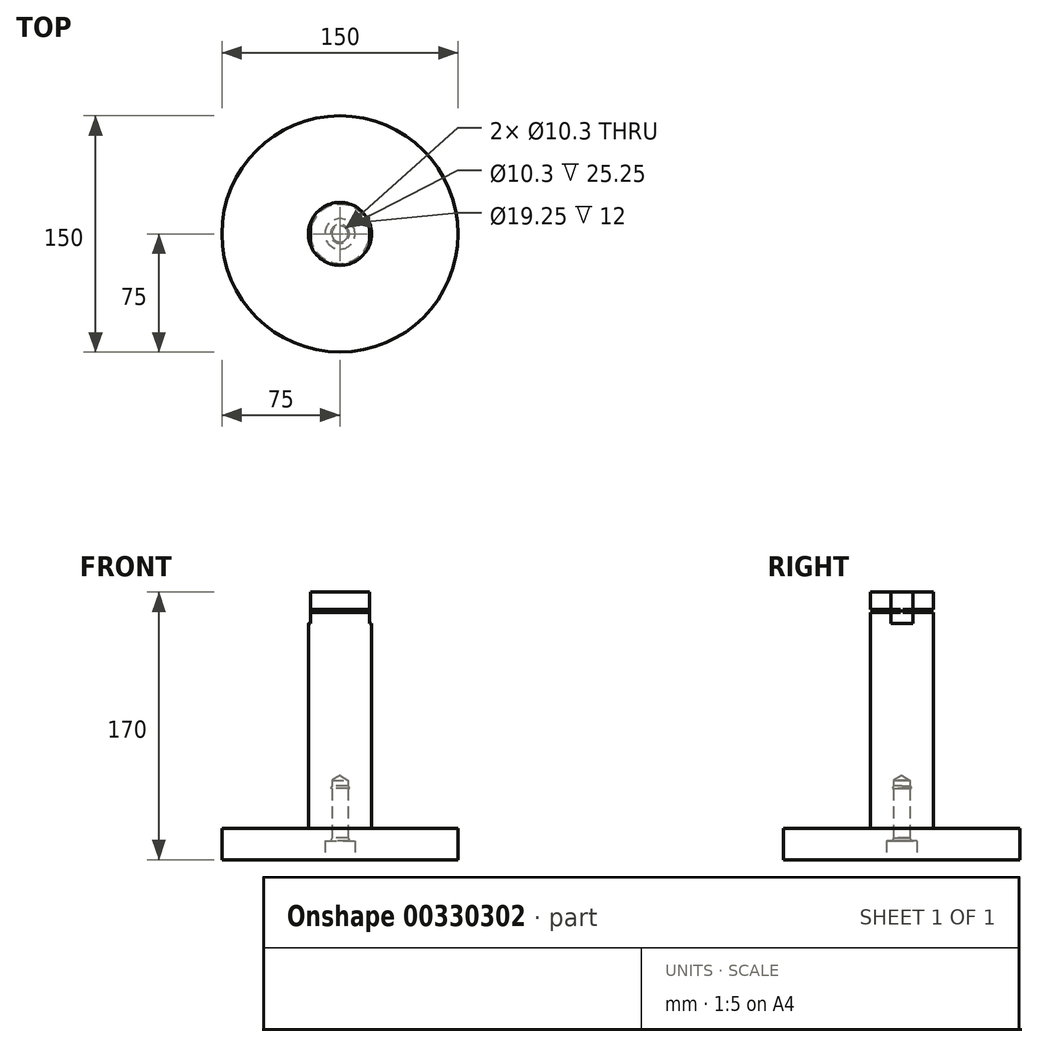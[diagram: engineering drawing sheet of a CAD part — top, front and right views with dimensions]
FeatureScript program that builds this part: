
annotation { "Feature Type Name" : "Feature", "Feature Type Description" : "" }
export const myFeature = defineFeature(function(context is Context, id is Id, definition is map)
    precondition{}
    {
        {
            var Q0;
            Q0=qCreatedBy(makeId("Top.planeOp"),FACE);
            var sketch = newSketch(context, id + "F0", { "sketchPlane" : qUnion([Q0])});
            skCircle(sketch, "E0", {"center": v(0, 0) * mm, "radius": 20 * mm});
            skCircle(sketch, "E1", {"center": v(0, 0) * mm, "radius": 75 * mm});
            skSolve(sketch);
        }
        {
            var Q0;
            Q0=makeQuery(id+"F0.imprint","IMPRINT",FACE,{"disambiguationData":[TD([[makeQuery(id+"F0.imprint","IMPRINT",EDGE,{"derivedFrom":sQuery(id+"F0.wireOp",EDGE,"E0")}),-1.0]])]});
            var Q1;
            Q1=makeQuery(id+"F0.imprint","IMPRINT",FACE,{"disambiguationData":[TD([[makeQuery(id+"F0.imprint","IMPRINT",EDGE,{"derivedFrom":sQuery(id+"F0.wireOp",EDGE,"E0")}),1.0]])]});
            extrude(context, id + "F1", {"entities" : qUnion([Q0, Q1]), "oppositeDirection" : true, "depth" : 20 * mm});
        }
        {
            var Q0;
            Q0=makeQuery(id+"F0.imprint","IMPRINT",FACE,{"disambiguationData":[TD([[makeQuery(id+"F0.imprint","IMPRINT",EDGE,{"derivedFrom":sQuery(id+"F0.wireOp",EDGE,"E0")}),1.0]])]});
            extrude(context, id + "F2", {"entities" : qUnion([Q0]), "depth" : 150 * mm});
        }
        {
            var Q0;
            Q0=makeQuery(id+"F1.opExtrude","CAP_FACE",FACE,{"disambiguationData":[OSD([sQuery(id+"F0.wireOp",EDGE,"E1")])],"isStart":false});
            var sketch = newSketch(context, id + "F3", { "sketchPlane" : qUnion([Q0])});
            skPoint(sketch, "E2", {"position": v(0, 0) * mm});
            skSolve(sketch);
        }
        {
            var Q0;
            Q0=sQuery(id+"F3.wireOp",VERTEX,"E2");
            var Q1;
            Q1=makeQuery(id+"F1.opExtrude","SWEPT_BODY",BODY,{"disambiguationData":[OSD([sQuery(id+"F0.wireOp",EDGE,"E1")])]});
            var Q2;
            Q2=makeQuery(id+"F2.opExtrude","SWEPT_BODY",BODY,{"disambiguationData":[OSD([sQuery(id+"F0.wireOp",EDGE,"E0")])]});
            hole(context, id + "F4", {"style" : HoleStyle.C_BORE, "endStyle" : HoleEndStyle.BLIND, "standardTappedOrClearance" : lookupTablePath({ "standard" : "ISO", "engagement" : "75%", "pitch" : "1.75 mm", "size" : "M12", "type" : "Tapped" }), "standardBlindInLast" : lookupTablePath({ "standard" : "ISO", "engagement" : "75%", "pitch" : "1.75 mm", "size" : "M12", "type" : "Tapped" }), "holeDiameter" : 10.3 * mm, "cBoreDiameter" : 19.25 * mm, "cBoreDepth" : 12 * mm, "showTappedDepth" : true, "holeDepth" : 50.5 * mm, "tappedDepth" : 47 * mm, "tapClearance" : 2, "locations" : qUnion([Q0]), "scope" : qUnion([Q1, Q2]), "majorDiameter" : 12 * mm});
        }
        {
            var Q0;
            Q0=qCreatedBy(makeId("Right.planeOp"),FACE);
            var sketch = newSketch(context, id + "F5", { "sketchPlane" : qUnion([Q0])});
            skLineSegment(sketch, "E3.0", {"start": v(9.62, -8) * mm, "end": v(-9.62, -8) * mm});
            skLineSegment(sketch, "E4", {"start": v(0, 0) * mm, "end": v(0, -13.23) * mm});
            skLineSegment(sketch, "E5", {"start": v(0, -8) * mm, "end": v(6, -8) * mm});
            skLineSegment(sketch, "E6.MirrorCS", {"start": v(0, -16) * mm, "end": v(0, -2.77) * mm});
            skLineSegment(sketch, "E7.MirrorCS", {"start": v(0, -8) * mm, "end": v(-6, -8) * mm});
            skLineSegment(sketch, "E8", {"start": v(5.15, -8) * mm, "end": v(5.15, -6.25) * mm});
            skLineSegment(sketch, "E9", {"start": v(5.15, -6.25) * mm, "end": v(6, -8) * mm});
            skLineSegment(sketch, "E10", {"start": v(6, -8) * mm, "end": v(5.15, -8) * mm});
            skLineSegment(sketch, "E11", {"start": v(0, -8) * mm, "end": v(0, 1.54) * mm});
            skLineSegment(sketch, "E12.0", {"start": v(-75, -20) * mm, "end": v(75, -20) * mm});
            skLineSegment(sketch, "E13", {"start": v(0, -20) * mm, "end": v(0, 27) * mm});
            skLineSegment(sketch, "E14", {"start": v(0, 27) * mm, "end": v(6, 27) * mm});
            skLineSegment(sketch, "E15", {"start": v(5.15, 25.25) * mm, "end": v(5.15, 27) * mm});
            skLineSegment(sketch, "E16", {"start": v(5.15, 27) * mm, "end": v(6, 25.25) * mm});
            skLineSegment(sketch, "E17", {"start": v(6, 25.25) * mm, "end": v(5.15, 25.25) * mm});
            skSolve(sketch);
        }
        {
            var Q0;
            Q0 = qSketchRegion(id + "F5", true);
            var Q1;
            Q1=sQuery(id+"F5.wireOp",EDGE,"E13");
            revolve(context, id + "F6", {"operationType" : NewBodyOperationType.REMOVE, "entities" : qUnion([Q0]), "axis" : qUnion([Q1]), "revolveType" : RevolveType.FULL, "oppositeDirection" : true});
        }
        {
            var Q0;
            Q0=makeQuery(id+"F2.opExtrude","CAP_FACE",FACE,{"disambiguationData":[OSD([sQuery(id+"F0.wireOp",EDGE,"E0")])],"isStart":false});
            var sketch = newSketch(context, id + "F7", { "sketchPlane" : qUnion([Q0])});
            skLineSegment(sketch, "E18", {"start": v(0, 0) * mm, "end": v(-20, 0) * mm});
            skLineSegment(sketch, "E19", {"start": v(-18.73, 7) * mm, "end": v(-18.73, 0) * mm});
            skLineSegment(sketch, "E20.MirrorCS", {"start": v(-18.73, -7) * mm, "end": v(-18.73, 0) * mm});
            skLineSegment(sketch, "E21.MirrorCS", {"start": v(18.73, 7) * mm, "end": v(18.73, 0) * mm});
            skLineSegment(sketch, "E22.MirrorCS", {"start": v(18.73, -7) * mm, "end": v(18.73, 0) * mm});
            skSolve(sketch);
        }
        {
            var Q0;
            {var subQ3=sQuery(id+"F7.wireOp",EDGE,"E19");Q0=makeQuery(id+"F7.imprint","IMPRINT",FACE,{"disambiguationData":[TD([[makeQuery(id+"F7.imprint","IMPRINT",EDGE,{"derivedFrom":subQ3}),-1.0]])]});}
            var Q1;
            {var subQ3=sQuery(id+"F7.wireOp",EDGE,"E20.MirrorCS");Q1=makeQuery(id+"F7.imprint","IMPRINT",FACE,{"disambiguationData":[TD([[makeQuery(id+"F7.imprint","IMPRINT",EDGE,{"derivedFrom":subQ3}),1.0]])]});}
            var Q2;
            {var subQ0=sQuery(id+"F7.wireOp",EDGE,"E21.MirrorCS");Q2=makeQuery(id+"F7.imprint","IMPRINT",FACE,{"disambiguationData":[TD([[makeQuery(id+"F7.imprint","IMPRINT",EDGE,{"derivedFrom":subQ0}),1.0]])]});}
            extrude(context, id + "F8", {"entities" : qUnion([Q0, Q1, Q2]), "operationType" : NewBodyOperationType.REMOVE, "oppositeDirection" : true, "depth" : 20 * mm});
        }
        {
            var Q0;
            Q0=makeQuery(id+"F0.imprint","IMPRINT",FACE,{"disambiguationData":[TD([[makeQuery(id+"F0.imprint","IMPRINT",EDGE,{"derivedFrom":sQuery(id+"F0.wireOp",EDGE,"E0")}),-1.0]])]});
            cPlane(context, id + "F9", {"entities" : qUnion([Q0]), "cplaneType" : CPlaneType.OFFSET, "offset" : 137 * mm, "width" : 150 * mm, "height" : 150 * mm});
        }
        {
            var Q0;
            Q0=qCreatedBy(id+"F9.planeOp",FACE);
            var sketch = newSketch(context, id + "F10", { "sketchPlane" : qUnion([Q0])});
            skCircle(sketch, "E23.0", {"center": v(0, 0) * mm, "radius": 20 * mm});
            skCircle(sketch, "E24", {"center": v(0, 0) * mm, "radius": 18.75 * mm});
            skSolve(sketch);
        }
        {
            var Q0;
            Q0=makeQuery(id+"F10.imprint","IMPRINT",FACE,{"disambiguationData":[TD([[makeQuery(id+"F10.imprint","IMPRINT",EDGE,{"derivedFrom":sQuery(id+"F10.wireOp",EDGE,"E23.0")}),1.0]])]});
            extrude(context, id + "F11", {"entities" : qUnion([Q0]), "operationType" : NewBodyOperationType.REMOVE, "depth" : 1.85 * mm});
        }
    });
